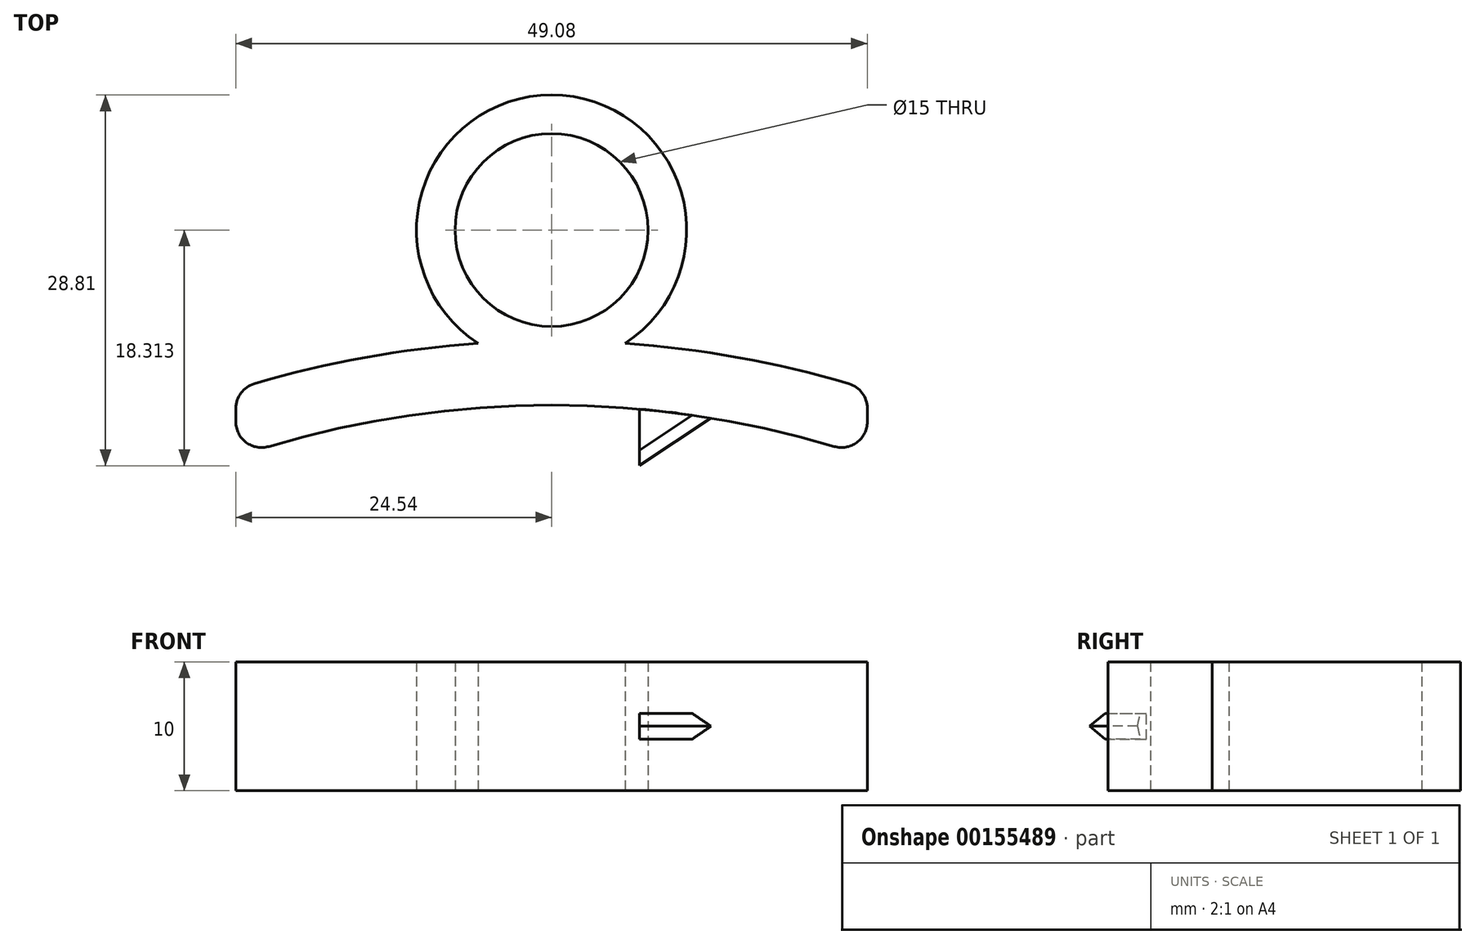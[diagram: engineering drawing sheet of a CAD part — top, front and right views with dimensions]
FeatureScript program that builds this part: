
annotation { "Feature Type Name" : "Feature", "Feature Type Description" : "" }
export const myFeature = defineFeature(function(context is Context, id is Id, definition is map)
    precondition{}
    {
        {
            var Q0;
            Q0=qCreatedBy(makeId("Top.planeOp"),FACE);
            var sketch = newSketch(context, id + "F0", { "sketchPlane" : qUnion([Q0])});
            skArc(sketch, "E0", {"start": v(21.97, -7.54) * mm, "mid": v(0, -4.32) * mm, "end": v(-21.97, -7.54) * mm});
            skArc(sketch, "E1.0", {"start": v(23.1, -2.66) * mm, "mid": v(0, 0.68) * mm, "end": v(-23.1, -2.66) * mm});
            skCircle(sketch, "E2", {"center": v(0, 9.28) * mm, "radius": 7.5 * mm});
            skCircle(sketch, "E3.0", {"center": v(0, 9.28) * mm, "radius": 10.5 * mm});
            skLineSegment(sketch, "E4", {"start": v(-10.5, 9.28) * mm, "end": v(-10.5, 0) * mm});
            skLineSegment(sketch, "E5", {"start": v(10.5, 9.28) * mm, "end": v(10.5, 0) * mm});
            skLineSegment(sketch, "E6", {"start": v(-24.54, -4.58) * mm, "end": v(-24.54, -5.62) * mm});
            skLineSegment(sketch, "E7", {"start": v(24.54, -4.58) * mm, "end": v(24.54, -5.62) * mm});
            skPoint(sketch, "E8.visualSharp", {"position": v(-24.54, -3.1) * mm});
            skArc(sketch, "E8.filletArc", {"start": v(-23.1, -2.66) * mm, "mid": v(-24.14, -3.38) * mm, "end": v(-24.54, -4.58) * mm});
            skPoint(sketch, "E9.visualSharp", {"position": v(-24.54, -8.35) * mm});
            skArc(sketch, "E9.filletArc", {"start": v(-24.54, -5.62) * mm, "mid": v(-23.74, -7.22) * mm, "end": v(-21.97, -7.54) * mm});
            skPoint(sketch, "E10.visualSharp", {"position": v(24.54, -3.1) * mm});
            skArc(sketch, "E10.filletArc", {"start": v(24.54, -4.58) * mm, "mid": v(24.14, -3.38) * mm, "end": v(23.1, -2.66) * mm});
            skPoint(sketch, "E11.visualSharp", {"position": v(24.54, -8.35) * mm});
            skArc(sketch, "E11.filletArc", {"start": v(21.97, -7.54) * mm, "mid": v(23.74, -7.22) * mm, "end": v(24.54, -5.62) * mm});
            skSolve(sketch);
        }
        {
            var Q0;
            Q0=makeQuery(id+"F0.imprint","IMPRINT",FACE,{"disambiguationData":[TD([[makeQuery(id+"F0.imprint","IMPRINT",EDGE,{"derivedFrom":sQuery(id+"F0.wireOp",EDGE,"E2")}),-1.0]])]});
            var Q1;
            {var subQ0=sQuery(id+"F0.wireOp",EDGE,"E3.0");var subQ1=sQuery(id+"F0.wireOp",EDGE,"E1.0");var subQ2=makeQuery(id+"F0.imprint","INTERSECT",VERTEX,{"disambiguationData":[OD(0.0)],"derivedFrom":[subQ1,subQ0]});Q1=makeQuery(id+"F0.imprint","IMPRINT",FACE,{"disambiguationData":[TD([[makeQuery(id+"F0.imprint","IMPRINT",EDGE,{"disambiguationData":[TD([[subQ2,-1.0]])],"derivedFrom":subQ1}),1.0]])]});}
            var Q2;
            Q2=makeQuery(id+"F0.imprint","IMPRINT",FACE,{"disambiguationData":[TD([[makeQuery(id+"F0.imprint","IMPRINT",EDGE,{"derivedFrom":sQuery(id+"F0.wireOp",EDGE,"E0")}),-1.0]])]});
            extrude(context, id + "F1", {"entities" : qUnion([Q0, Q1, Q2]), "depth" : 10 * mm});
        }
        {
            var Q0;
            Q0=makeQuery(id+"F1.opExtrude","CAP_FACE",FACE,{"disambiguationData":[OSD([sQuery(id+"F0.wireOp",EDGE,"E0"),sQuery(id+"F0.wireOp",EDGE,"E1.0"),sQuery(id+"F0.wireOp",EDGE,"E2"),sQuery(id+"F0.wireOp",EDGE,"E3.0"),sQuery(id+"F0.wireOp",EDGE,"E6"),sQuery(id+"F0.wireOp",EDGE,"E7"),sQuery(id+"F0.wireOp",EDGE,"E8.filletArc"),sQuery(id+"F0.wireOp",EDGE,"E9.filletArc"),sQuery(id+"F0.wireOp",EDGE,"E10.filletArc"),sQuery(id+"F0.wireOp",EDGE,"E11.filletArc")])],"isStart":false});
            cPlane(context, id + "F2", {"entities" : qUnion([Q0]), "cplaneType" : CPlaneType.OFFSET, "offset" : 4 * mm, "oppositeDirection" : true, "width" : 150 * mm, "height" : 150 * mm});
        }
        {
            var Q0;
            Q0=qCreatedBy(id+"F2.planeOp",FACE);
            var sketch = newSketch(context, id + "F3", { "sketchPlane" : qUnion([Q0])});
            skArc(sketch, "E12.0", {"start": v(21.97, -7.54) * mm, "mid": v(0, -4.32) * mm, "end": v(-21.97, -7.54) * mm});
            skLineSegment(sketch, "E13", {"start": v(13.1, -5.45) * mm, "end": v(6.84, -9.63) * mm});
            skLineSegment(sketch, "E14", {"start": v(6.84, -9.63) * mm, "end": v(6.84, -4.63) * mm});
            skSolve(sketch);
        }
        {
            var Q0;
            {var subQ0=sQuery(id+"F3.wireOp",EDGE,"E13");Q0=makeQuery(id+"F3.imprint","IMPRINT",FACE,{"disambiguationData":[TD([[makeQuery(id+"F3.imprint","IMPRINT",EDGE,{"derivedFrom":subQ0}),-1.0]])]});}
            extrude(context, id + "F4", {"entities" : qUnion([Q0]), "operationType" : NewBodyOperationType.ADD, "oppositeDirection" : true, "depth" : 2 * mm});
        }
        {
            var Q0;
            Q0=makeQuery(id+"F4.opExtrude","CAP_EDGE",EDGE,{"disambiguationData":[OSD([sQuery(id+"F3.wireOp",EDGE,"E13")])],"isStart":true});
            var Q1;
            Q1=makeQuery(id+"F4.opExtrude","CAP_EDGE",EDGE,{"disambiguationData":[OSD([sQuery(id+"F3.wireOp",EDGE,"E13")])],"isStart":false});
            chamfer(context, id + "F5", {"entities" : qUnion([Q0, Q1]), "width" : 1.5 * mm, "tangentPropagation" : true});
        }
    });
